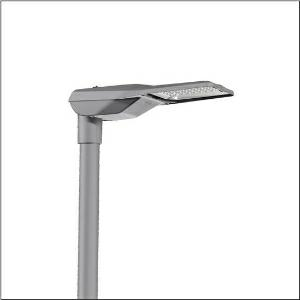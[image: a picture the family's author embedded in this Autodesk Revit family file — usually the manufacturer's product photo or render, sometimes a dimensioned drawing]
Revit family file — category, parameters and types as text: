
# Revit family: streetlight_sl_21_mini___st0_8a_5xe2c43s08gb_a339
name_source: partatom
category: Lighting Fixtures
units: mm (PartAtom-declared; Revit-internal decimal feet)

## family parameters
Cut with Voids When Loaded = No
Host = Face
Light Source = No
Part Type = Normal
Room Calculation Point = No
Round Connector Dimension = Use Diameter
Shared = No

## types (1)
- --- (1 x LED, 6180 lm, 40.4 W, 4000K)
    Apparent Load = 40 VA
    CIE Flux Codes = 38 75 97 100 100
    Color Rendering = 70
    Color Temperature = 4000K
    Default Elevation = 1800 mm
    Description = Streetlight SL 21 mini, mast luminaire, primary light control with lens, of PMMA, primary optical cover: cover, of toughened safety glass, transparent, light distribution: ST0.8a, light emission: direct distribution, primary light characteristic: asymmetric, installation type: side-entry, post-top, LED, High Power LED, rated luminous flux: 6.180lm, luminous efficacy: 153lm/W, light colour: 740, colour temperature: 4000K, control gear: D4i, control: overheat protection, constant luminous flux control, time-dependent luminous flux control, flexible luminous flux parameterisation, pre-setting: logarithmic dimming characteristic, mains connection: 220..240V, AC, 50/60Hz, start of lifetime: 40W, end of service life: 41W, reduction: 19W, luminaire housing, of diecast aluminium, powder-coated, SITECO metallic grey (DB 702S), corrosivity category C5 high according to DIN EN ISO 12944, please order mast flange separately, inclination adjustable: 0°, 5°, 10°, 15°, sealing non-destructively replaceable, multi-level sealing system, length: 628mm, width: 235mm, height: 110mm, mast flange for spigot size: 42mm (side-entry): 5XC10008XM4, 60/48mm (side-entry/post-top): 5XC10108XM2, 76/60mm (side-entry/post-top): 5XC10108XM1, mounting height: 4..8m, Smart Interface above, protection rating (complete): IP66, insulation class (complete): insulation class II (safety insulation), certification: CE, ENEC, ENEC+, VDE, impact resistance: IK10, permissible operating ambient temperature for outdoor applications: -40..+50°C, standard-compliant lighting for roads and squares, packaging unit: 1 piece

Light Distribution: ST0.8a
    Height = 110 mm
    Lamp = 1 x LED
    Lamp Light Flux = 6180 lm
    Lamp Power = 40.4 W
    Lamp count = 1
    Length = 625 mm
    Luminous efficacy = 153 lm/W
    Manufacturer = Siteco
    ModVariant = No
    Model = 5XE2C43S08GB
    Number of Poles = 1
    OnlyDefault = Yes
    Power Factor = 1
    Product Name = Streetlight SL 21 mini | ST0.8a
    Product group = mast luminaire | pylon top
    ProductGroupID = 6100
    Protection Class = Protection class II
    Protection Degree = IP 66
    RLX_Detail_Level = 1
    RLX_Emergency_Light_Flux = 0 lm
    RLX_Emergency_Type = 0
    RLX_Emergency_Type_DB = No
    RlxData = <blob elided: 26245 chars, md5=bc08d538>
    Socket = socket
    Standby Power = 0 W
    System Light Flux = 6180 lm
    System Power = 40 W
    Type Comments = factory setting: luminous flux: 100 % | dim-lin: 254 | 812 mA
    Type Image = l_1003515.jpg
    URL = http://relux.com
    VarID = @adj_182991
    Voltage = 0 V
    Weight = 0.00 kg
    Width = 234 mm

## geometry (parser evidence)
native form markers: Blend x4, Sweep x10
no freeform markers — native parametric forms only
